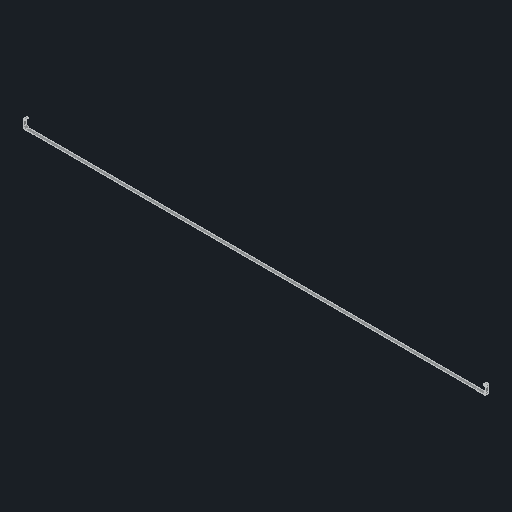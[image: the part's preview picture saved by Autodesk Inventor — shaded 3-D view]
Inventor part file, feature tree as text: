
AUTODESK INVENTOR PART (.ipt)
format: ipt  version: 2024.2 (Build 282272000, 272)  size: 134,144 bytes
history: native  units: in
note: dims shown in document units (in); Inventor stores cm internally (conversion verified against a paired STEP export)
features: mirror x1
ambient origin geometry x8: Origin, YZ Plane, XZ Plane, XY Plane, X Axis, Y Axis, Z Axis, Center Point
bodies: Solid1 (feature_tree)
feature tree (1):
  mirror  "Mirror1"
